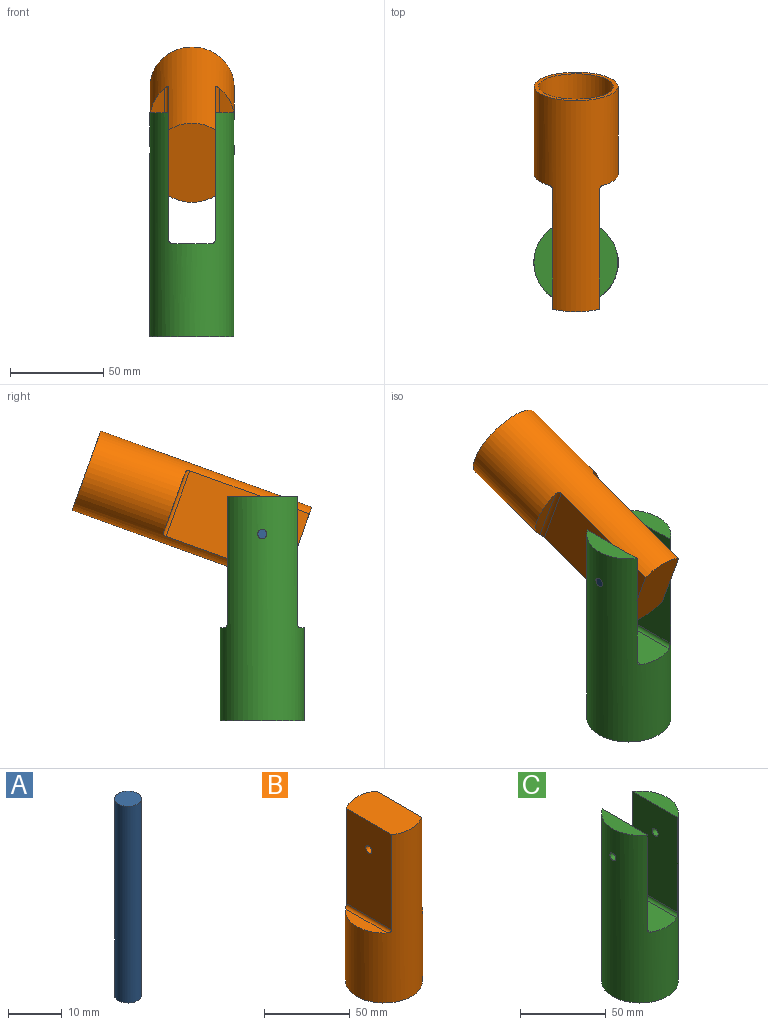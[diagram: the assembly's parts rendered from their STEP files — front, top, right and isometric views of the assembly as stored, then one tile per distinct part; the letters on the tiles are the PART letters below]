
ASSEMBLY  parts=3 mates=2
PART A: 3 faces, bbox 5x5x45 mm
  f0: cylinder r=2.5mm len=45mm, axis (0,0,-1), area 706.9mm2, adj f1,f2
  f1: plane 5x5mm, normal (0,0,1), area 19.6mm2, adj f0
  f2: plane 5x5mm, normal (0,0,-1), area 19.6mm2, adj f0
PART B: 12 faces, bbox 45x45x120 mm
  f0: plane 45x25mm, normal (0,0,1), area 1064.1mm2, adj f1,f3,f5
  f1: cylinder r=22.5mm len=120mm, axis (0,0,-1), area 10783.7mm2, adj f0,f2,f3,f4,f5,f6,f10,f11
  f2: plane 45x45mm, normal (0,0,-1), area 333.8mm2, adj f1,f7
  f3: plane 68x37.42mm, normal (-1,0,0), area 2524.7mm2, adj f0,f1,f9,f10
  f4: plane 34.41x8mm, normal (0,0,1), area 191.2mm2, adj f1,f10
  f5: plane 68x37.42mm, normal (1,0,0), area 2524.7mm2, adj f0,f1,f9,f11
  f6: plane 34.41x8mm, normal (0,0,1), area 191.2mm2, adj f1,f11
  f7: cylinder r=20mm len=40mm, axis (0,0,-1), area 4398.2mm2, adj f2,f8
  f8: plane 40x40mm, normal (0,0,-1), area 1256.6mm2, adj f7
  f9: cylinder r=2.5mm len=25mm, axis (1,0,0), area 392.7mm2, adj f3,f5
  f10: cylinder r=2mm len=37.42mm, axis (0,1,0), area 114.3mm2, adj f1,f3,f4
  f11: cylinder r=2mm len=37.42mm, axis (0,-1,0), area 114.3mm2, adj f1,f5,f6
PART C: 13 faces, bbox 45x45x120 mm
  f0: cylinder r=22.5mm len=120mm, axis (0,0,-1), area 13218.5mm2, adj f1,f2,f3,f4,f5,f6,f9,f10
  f1: plane 37.42x10mm, normal (0,0,1), area 263.2mm2, adj f0,f5
  f2: plane 37.42x10mm, normal (0,0,1), area 263.2mm2, adj f0,f4
  f3: plane 45x45mm, normal (0,0,-1), area 333.8mm2, adj f0,f7
  f4: plane 68x37.42mm, normal (1,0,0), area 2524.7mm2, adj f0,f2,f10,f11
  f5: plane 68x37.42mm, normal (-1,0,0), area 2524.7mm2, adj f0,f1,f9,f12
  f6: plane 45x21mm, normal (0,0,1), area 909.5mm2, adj f0,f11,f12
  f7: cylinder r=20mm len=40mm, axis (0,0,-1), area 4398.2mm2, adj f3,f8
  f8: plane 40x40mm, normal (0,0,-1), area 1256.6mm2, adj f7
  f9: cylinder r=2.5mm len=10mm, axis (1,0,0), area 156mm2, adj f0,f5
  f10: cylinder r=2.5mm len=10mm, axis (1,0,0), area 156mm2, adj f0,f4
  f11: cylinder r=2mm len=39.8mm, axis (0,-1,0), area 120.4mm2, adj f0,f4,f6
  f12: cylinder r=2mm len=39.8mm, axis (0,1,0), area 120.4mm2, adj f0,f5,f6
PLACE A rot(axis=(0.71,0,0.71),180deg) t=(-6.17,38.95,84.34)mm
PLACE B rot(axis=(1,0,0),109.9deg) t=(16.33,133.01,118.31)mm
PLACE C t=(16.26,38.95,-15.66)mm fixed
MATE fastened C.f9 <-> A.f0  axis (1,0,0) through (38.83,38.95,84.34)mm
MATE revolute A.f0 <-> B.f9  axis (-1,0,0) through (16.33,38.95,84.34)mm
